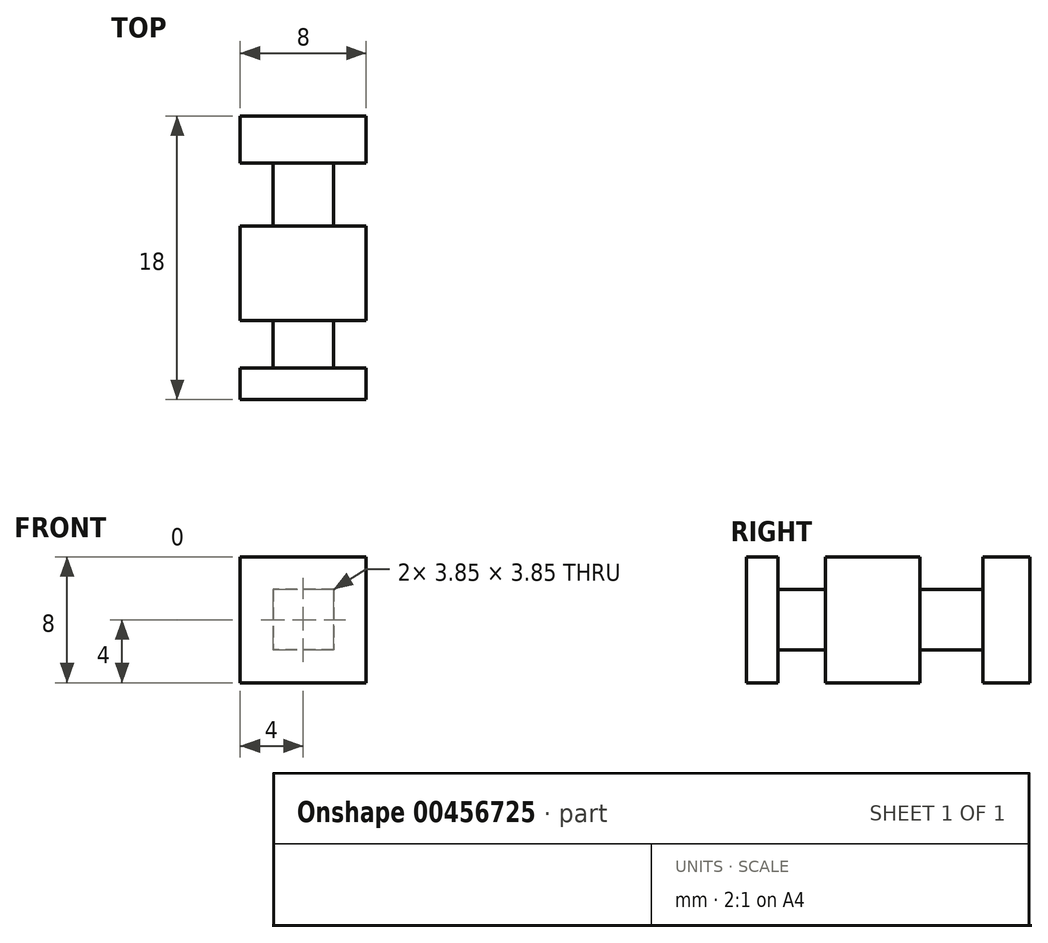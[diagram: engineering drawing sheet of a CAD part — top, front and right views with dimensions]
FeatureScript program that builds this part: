
annotation { "Feature Type Name" : "Feature", "Feature Type Description" : "" }
export const myFeature = defineFeature(function(context is Context, id is Id, definition is map)
    precondition{}
    {
        {
            var Q0;
            Q0=qCreatedBy(makeId("Top.planeOp"),FACE);
            var sketch = newSketch(context, id + "F0", { "sketchPlane" : qUnion([Q0])});
            skLineSegment(sketch, "E0.bottom", {"start": v(4, 3) * mm, "end": v(-4, 3) * mm});
            skLineSegment(sketch, "E0.top", {"start": v(4, -3) * mm, "end": v(-4, -3) * mm});
            skLineSegment(sketch, "E0.left", {"start": v(4, 3) * mm, "end": v(4, -3) * mm});
            skLineSegment(sketch, "E0.right", {"start": v(-4, 3) * mm, "end": v(-4, -3) * mm});
            skPoint(sketch, "E0.middle", {"position": v(0, 0) * mm});
            skSolve(sketch);
        }
        {
            var Q0;
            Q0=makeQuery(id+"F0.imprint","IMPRINT",FACE,{"disambiguationData":[TD([[makeQuery(id+"F0.imprint","IMPRINT",EDGE,{"derivedFrom":sQuery(id+"F0.wireOp",EDGE,"E0.bottom")}),1.0]])]});
            extrude(context, id + "F1", {"entities" : qUnion([Q0]), "depth" : 8 * mm});
        }
        {
            var Q0;
            Q0=makeQuery(id+"F1.opExtrude","SWEPT_FACE",FACE,{"disambiguationData":[OSD([sQuery(id+"F0.wireOp",EDGE,"E0.top")])]});
            var sketch = newSketch(context, id + "F2", { "sketchPlane" : qUnion([Q0])});
            skLineSegment(sketch, "E1.bottom", {"start": v(1.93, 5.93) * mm, "end": v(-1.93, 5.93) * mm});
            skLineSegment(sketch, "E1.top", {"start": v(1.93, 2.08) * mm, "end": v(-1.92, 2.08) * mm});
            skLineSegment(sketch, "E1.left", {"start": v(1.93, 5.93) * mm, "end": v(1.93, 2.08) * mm});
            skLineSegment(sketch, "E1.right", {"start": v(-1.93, 5.93) * mm, "end": v(-1.92, 2.08) * mm});
            skPoint(sketch, "E1.middle", {"position": v(0, 4) * mm});
            skSolve(sketch);
        }
        {
            var Q0;
            Q0 = qSketchRegion(id + "F2", true);
            extrude(context, id + "F3", {"entities" : qUnion([Q0]), "operationType" : NewBodyOperationType.ADD, "depth" : 3 * mm});
        }
        {
            var Q0;
            Q0=makeQuery(id+"F3.opExtrude","CAP_FACE",FACE,{"disambiguationData":[OSD([sQuery(id+"F2.wireOp",EDGE,"E1.bottom"),sQuery(id+"F2.wireOp",EDGE,"E1.top"),sQuery(id+"F2.wireOp",EDGE,"E1.left"),sQuery(id+"F2.wireOp",EDGE,"E1.right")])],"isStart":false});
            var sketch = newSketch(context, id + "F4", { "sketchPlane" : qUnion([Q0])});
            skLineSegment(sketch, "E2.bottom", {"start": v(4, 8) * mm, "end": v(-4, 8) * mm});
            skLineSegment(sketch, "E2.top", {"start": v(4, 0) * mm, "end": v(-4, 0) * mm});
            skLineSegment(sketch, "E2.left", {"start": v(4, 8) * mm, "end": v(4, 0) * mm});
            skLineSegment(sketch, "E2.right", {"start": v(-4, 8) * mm, "end": v(-4, 0) * mm});
            skPoint(sketch, "E2.middle", {"position": v(0, 4) * mm});
            skPoint(sketch, "E2.middle.positionSnap0", {"position": v(-1.92, 4) * mm});
            skPoint(sketch, "E2.centerSnap0", {"position": v(-1.92, 4) * mm});
            skSolve(sketch);
        }
        {
            var Q0;
            Q0=makeQuery(id+"F4.imprint","IMPRINT",FACE,{"disambiguationData":[TD([[makeQuery(id+"F4.imprint","IMPRINT",EDGE,{"derivedFrom":sQuery(id+"F4.wireOp",EDGE,"E2.bottom")}),1.0]])]});
            var Q1;
            Q1=makeQuery(id+"F4.imprint","IMPRINT",FACE,{"disambiguationData":[TD([[makeQuery(id+"F4.imprint","IMPRINT",EDGE,{"derivedFrom":makeQuery(id+"F3.opExtrude","CAP_EDGE",EDGE,{"disambiguationData":[OSD([sQuery(id+"F2.wireOp",EDGE,"E1.bottom")])],"isStart":false})}),1.0]])]});
            extrude(context, id + "F5", {"entities" : qUnion([Q0, Q1]), "operationType" : NewBodyOperationType.ADD, "depth" : 2 * mm});
        }
        {
            var Q0;
            Q0=makeQuery(id+"F1.opExtrude","SWEPT_FACE",FACE,{"disambiguationData":[OSD([sQuery(id+"F0.wireOp",EDGE,"E0.bottom")])]});
            var sketch = newSketch(context, id + "F6", { "sketchPlane" : qUnion([Q0])});
            skLineSegment(sketch, "E3.bottom", {"start": v(1.93, 5.92) * mm, "end": v(-1.93, 5.92) * mm});
            skLineSegment(sketch, "E3.top", {"start": v(1.93, 2.07) * mm, "end": v(-1.92, 2.07) * mm});
            skLineSegment(sketch, "E3.left", {"start": v(1.93, 5.92) * mm, "end": v(1.93, 2.07) * mm});
            skLineSegment(sketch, "E3.right", {"start": v(-1.93, 5.92) * mm, "end": v(-1.92, 2.07) * mm});
            skPoint(sketch, "E3.middle", {"position": v(0, 4) * mm});
            skPoint(sketch, "E3.middle.positionSnap0", {"position": v(4, 4) * mm});
            skPoint(sketch, "E3.centerSnap0", {"position": v(4, 4) * mm});
            skSolve(sketch);
        }
        {
            var Q0;
            Q0=makeQuery(id+"F6.imprint","IMPRINT",FACE,{"disambiguationData":[TD([[makeQuery(id+"F6.imprint","IMPRINT",EDGE,{"derivedFrom":sQuery(id+"F6.wireOp",EDGE,"E3.bottom")}),1.0]])]});
            var sketch = newSketch(context, id + "F7", { "sketchPlane" : qUnion([Q0])});
            skSolve(sketch);
        }
        {
            var Q0;
            Q0=makeQuery(id+"F7.imprint","IMPRINT",FACE,{"disambiguationData":[TD([[makeQuery(id+"F7.imprint","IMPRINT",EDGE,{"derivedFrom":makeQuery(id+"F6.imprint","IMPRINT",EDGE,{"derivedFrom":sQuery(id+"F6.wireOp",EDGE,"E3.bottom")})}),1.0]])]});
            extrude(context, id + "F8", {"entities" : qUnion([Q0]), "operationType" : NewBodyOperationType.ADD, "depth" : 3 * mm});
        }
        {
            var Q0;
            Q0=makeQuery(id+"F8.opExtrude","CAP_FACE",FACE,{"disambiguationData":[OSD([sQuery(id+"F6.wireOp",EDGE,"E3.bottom"),sQuery(id+"F6.wireOp",EDGE,"E3.top"),sQuery(id+"F6.wireOp",EDGE,"E3.left"),sQuery(id+"F6.wireOp",EDGE,"E3.right")])],"isStart":false});
            var sketch = newSketch(context, id + "F9", { "sketchPlane" : qUnion([Q0])});
            skLineSegment(sketch, "E4.bottom", {"start": v(4, 8) * mm, "end": v(-4, 8) * mm});
            skLineSegment(sketch, "E4.top", {"start": v(4, 0) * mm, "end": v(-4, 0) * mm});
            skLineSegment(sketch, "E4.left", {"start": v(4, 8) * mm, "end": v(4, 0) * mm});
            skLineSegment(sketch, "E4.right", {"start": v(-4, 8) * mm, "end": v(-4, 0) * mm});
            skPoint(sketch, "E4.middle", {"position": v(0, 4) * mm});
            skPoint(sketch, "E4.middle.positionSnap0", {"position": v(1.93, 4) * mm});
            skPoint(sketch, "E4.centerSnap0", {"position": v(1.93, 4) * mm});
            skSolve(sketch);
        }
        {
            var Q0;
            Q0=makeQuery(id+"F9.imprint","IMPRINT",FACE,{"disambiguationData":[TD([[makeQuery(id+"F9.imprint","IMPRINT",EDGE,{"derivedFrom":sQuery(id+"F9.wireOp",EDGE,"E4.bottom")}),1.0]])]});
            var Q1;
            Q1=makeQuery(id+"F9.imprint","IMPRINT",FACE,{"disambiguationData":[TD([[makeQuery(id+"F9.imprint","IMPRINT",EDGE,{"derivedFrom":makeQuery(id+"F8.opExtrude","CAP_EDGE",EDGE,{"disambiguationData":[OSD([sQuery(id+"F6.wireOp",EDGE,"E3.bottom")])],"isStart":false})}),1.0]])]});
            extrude(context, id + "F10", {"entities" : qUnion([Q0, Q1]), "operationType" : NewBodyOperationType.ADD, "depth" : 2.35 * mm});
        }
        {
            var Q0;
            Q0=makeQuery(id+"F10.opExtrude","CAP_FACE",FACE,{"disambiguationData":[OSD([sQuery(id+"F9.wireOp",EDGE,"E4.bottom"),sQuery(id+"F9.wireOp",EDGE,"E4.top"),sQuery(id+"F9.wireOp",EDGE,"E4.left"),sQuery(id+"F9.wireOp",EDGE,"E4.right")])],"isStart":true});
            extrude(context, id + "F11", {"entities" : qUnion([Q0]), "operationType" : NewBodyOperationType.ADD, "oppositeDirection" : true, "depth" : .35 * mm});
        }
        {
            var Q0;
            Q0=makeQuery(id+"F10.opExtrude","CAP_FACE",FACE,{"disambiguationData":[OSD([sQuery(id+"F9.wireOp",EDGE,"E4.bottom"),sQuery(id+"F9.wireOp",EDGE,"E4.top"),sQuery(id+"F9.wireOp",EDGE,"E4.left"),sQuery(id+"F9.wireOp",EDGE,"E4.right")])],"isStart":true});
            extrude(context, id + "F12", {"entities" : qUnion([Q0]), "operationType" : NewBodyOperationType.REMOVE, "oppositeDirection" : true, "depth" : 1 * mm});
        }
        {
            var Q0;
            Q0=makeQuery(id+"F10.opExtrude","CAP_FACE",FACE,{"disambiguationData":[OSD([sQuery(id+"F9.wireOp",EDGE,"E4.bottom"),sQuery(id+"F9.wireOp",EDGE,"E4.top"),sQuery(id+"F9.wireOp",EDGE,"E4.left"),sQuery(id+"F9.wireOp",EDGE,"E4.right")])],"isStart":false});
            extrude(context, id + "F13", {"entities" : qUnion([Q0]), "operationType" : NewBodyOperationType.ADD, "depth" : .65 * mm});
        }
        {
            var Q0;
            Q0=makeQuery(id+"F13.opExtrude","CAP_FACE",FACE,{"disambiguationData":[OSD([sQuery(id+"F9.wireOp",EDGE,"E4.bottom"),sQuery(id+"F9.wireOp",EDGE,"E4.top"),sQuery(id+"F9.wireOp",EDGE,"E4.left"),sQuery(id+"F9.wireOp",EDGE,"E4.right")])],"isStart":false});
            extrude(context, id + "F14", {"entities" : qUnion([Q0]), "operationType" : NewBodyOperationType.ADD, "depth" : 1 * mm});
        }
    });
